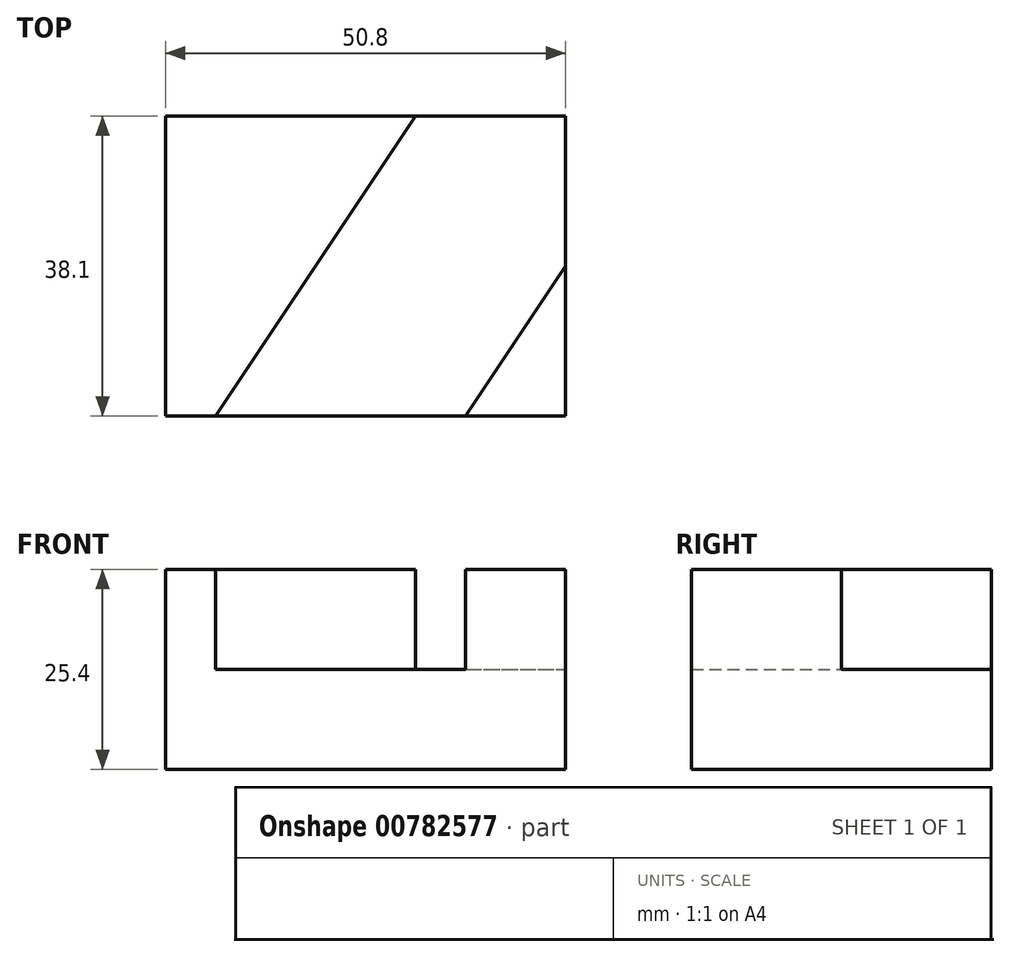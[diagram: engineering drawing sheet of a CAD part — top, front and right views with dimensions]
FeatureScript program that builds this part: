
annotation { "Feature Type Name" : "Feature", "Feature Type Description" : "" }
export const myFeature = defineFeature(function(context is Context, id is Id, definition is map)
    precondition{}
    {
        {
            var Q0;
            Q0=qCreatedBy(makeId("Front.planeOp"),FACE);
            var sketch = newSketch(context, id + "F0", { "sketchPlane" : qUnion([Q0])});
            skLineSegment(sketch, "E0", {"start": v(0, 0) * mm, "end": v(0, 25.4) * mm});
            skLineSegment(sketch, "E1", {"start": v(0, 25.4) * mm, "end": v(6.35, 25.4) * mm});
            skLineSegment(sketch, "E2", {"start": v(6.35, 25.4) * mm, "end": v(6.35, 12.7) * mm});
            skLineSegment(sketch, "E3", {"start": v(6.35, 12.7) * mm, "end": v(38.1, 12.7) * mm});
            skLineSegment(sketch, "E4", {"start": v(38.1, 12.7) * mm, "end": v(38.1, 25.4) * mm});
            skLineSegment(sketch, "E5", {"start": v(38.1, 25.4) * mm, "end": v(50.8, 25.4) * mm});
            skLineSegment(sketch, "E6", {"start": v(50.8, 25.4) * mm, "end": v(50.8, 0) * mm});
            skLineSegment(sketch, "E7", {"start": v(50.8, 0) * mm, "end": v(0, 0) * mm});
            skLineSegment(sketch, "E8", {"start": v(0, 25.4) * mm, "end": v(31.75, 25.4) * mm});
            skLineSegment(sketch, "E9", {"start": v(31.75, 25.4) * mm, "end": v(31.75, 12.7) * mm});
            skSolve(sketch);
        }
        {
            var Q0;
            Q0=makeQuery(id+"F0.imprint","IMPRINT",FACE,{"disambiguationData":[TD([[makeQuery(id+"F0.imprint","IMPRINT",EDGE,{"derivedFrom":sQuery(id+"F0.wireOp",EDGE,"E0")}),-1.0]])]});
            extrude(context, id + "F1", {"entities" : qUnion([Q0]), "depth" : 25.4 * mm, "offsetDistance" : 25.4 * mm});
        }
        {
            var Q0;
            Q0 = qSketchRegion(id + "F0", true);
            extrude(context, id + "F2", {"entities" : qUnion([Q0]), "operationType" : NewBodyOperationType.ADD, "depth" : 38.1 * mm, "offsetDistance" : 25.4 * mm});
        }
        {
            var Q0;
            {var subQ0=sQuery(id+"F0.wireOp",EDGE,"E6");Q0=makeQuery(id+"F2.boolean.opBoolean","MERGE",FACE,{"derivedFrom":[makeQuery(id+"F1.opExtrude","SWEPT_FACE",FACE,{"disambiguationData":[OSD([subQ0])]}),makeQuery(id+"F2.opExtrude","SWEPT_FACE",FACE,{"disambiguationData":[OSD([subQ0])]})]});}
            var sketch = newSketch(context, id + "F3", { "sketchPlane" : qUnion([Q0])});
            skLineSegment(sketch, "E10", {"start": v(0, 0) * mm, "end": v(0, 12.7) * mm});
            skLineSegment(sketch, "E11", {"start": v(0, 12.7) * mm, "end": v(-19.05, 12.7) * mm});
            skLineSegment(sketch, "E12", {"start": v(-19.05, 12.7) * mm, "end": v(-19.05, 25.4) * mm});
            skSolve(sketch);
        }
        {
            var Q0;
            {var subQ0=sQuery(id+"F3.wireOp",EDGE,"E11");Q0=makeQuery(id+"F3.imprint","IMPRINT",FACE,{"disambiguationData":[TD([[makeQuery(id+"F3.imprint","IMPRINT",EDGE,{"derivedFrom":subQ0}),-1.0]])]});}
            extrude(context, id + "F4", {"entities" : qUnion([Q0]), "operationType" : NewBodyOperationType.REMOVE, "oppositeDirection" : true, "depth" : 19.05 * mm, "offsetDistance" : 25.4 * mm});
        }
        {
            var Q0;
            {var subQ0=sQuery(id+"F0.wireOp",EDGE,"E5");Q0=makeQuery(id+"F2.boolean.opBoolean","MERGE",FACE,{"derivedFrom":[makeQuery(id+"F1.opExtrude","SWEPT_FACE",FACE,{"disambiguationData":[OSD([subQ0])]}),makeQuery(id+"F2.opExtrude","SWEPT_FACE",FACE,{"disambiguationData":[OSD([subQ0])]})]});}
            var sketch = newSketch(context, id + "F5", { "sketchPlane" : qUnion([Q0])});
            skLineSegment(sketch, "E13", {"start": v(38.1, -38.1) * mm, "end": v(50.8, -19.05) * mm});
            skSolve(sketch);
        }
        {
            var Q0;
            {var subQ0=sQuery(id+"F0.wireOp",EDGE,"E8");Q0=makeQuery(id+"F2.boolean.opBoolean","MERGE",FACE,{"derivedFrom":[makeQuery(id+"F1.opExtrude","SWEPT_FACE",FACE,{"disambiguationData":[OSD([subQ0])]}),makeQuery(id+"F2.opExtrude","SWEPT_FACE",FACE,{"disambiguationData":[OSD([subQ0])]})]});}
            var sketch = newSketch(context, id + "F6", { "sketchPlane" : qUnion([Q0])});
            skLineSegment(sketch, "E14", {"start": v(0, -38.1) * mm, "end": v(6.35, -38.1) * mm});
            skLineSegment(sketch, "E15", {"start": v(6.35, -38.1) * mm, "end": v(31.75, 0) * mm});
            skSolve(sketch);
        }
        {
            var Q0;
            {var subQ0=sQuery(id+"F6.wireOp",EDGE,"E15");Q0=makeQuery(id+"F6.imprint","IMPRINT",FACE,{"disambiguationData":[TD([[makeQuery(id+"F6.imprint","IMPRINT",EDGE,{"derivedFrom":subQ0}),-1.0]])]});}
            var Q1;
            Q1=makeQuery(id+"F5.imprint","IMPRINT",FACE,{"disambiguationData":[TD([[makeQuery(id+"F5.imprint","IMPRINT",EDGE,{"derivedFrom":sQuery(id+"F5.wireOp",EDGE,"E13")}),1.0]])]});
            extrude(context, id + "F7", {"entities" : qUnion([Q0, Q1]), "operationType" : NewBodyOperationType.REMOVE, "oppositeDirection" : true, "depth" : 12.7 * mm, "offsetDistance" : 25.4 * mm});
        }
    });
